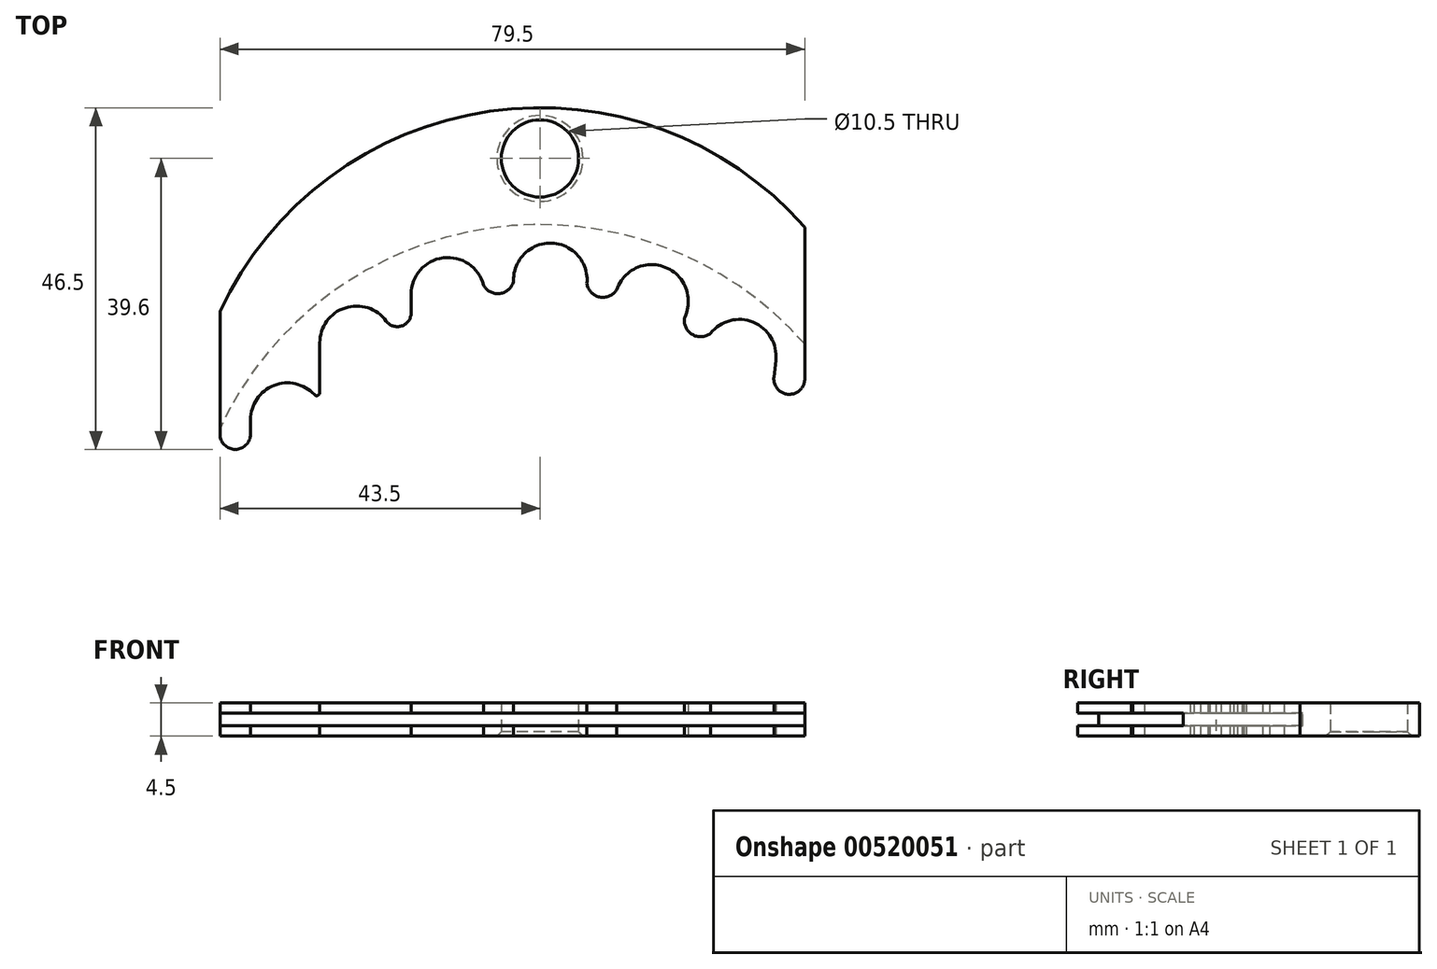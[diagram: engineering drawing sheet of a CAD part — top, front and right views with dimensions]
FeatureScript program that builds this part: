
annotation { "Feature Type Name" : "Feature", "Feature Type Description" : "" }
export const myFeature = defineFeature(function(context is Context, id is Id, definition is map)
    precondition{}
    {
        {
            var Q0;
            Q0=qCreatedBy(makeId("Top.planeOp"),FACE);
            var sketch = newSketch(context, id + "F0", { "sketchPlane" : qUnion([Q0])});
            skCircle(sketch, "E0", {"center": v(0, 0) * mm, "radius": 13 * mm, "construction": true});
            skCircle(sketch, "E1", {"center": v(0, 0) * mm, "radius": 13.5 * mm, "construction": true});
            skCircle(sketch, "E2", {"center": v(0, 0) * mm, "radius": 16 * mm, "construction": true});
            skLineSegment(sketch, "E3", {"start": v(0, 0) * mm, "end": v(0.47, 13.5) * mm, "construction": true});
            skLineSegment(sketch, "E4", {"start": v(0, 0) * mm, "end": v(5.06, 12.52) * mm, "construction": true});
            skLineSegment(sketch, "E5", {"start": v(0, 0) * mm, "end": v(9.03, 10.03) * mm, "construction": true});
            skLineSegment(sketch, "E6", {"start": v(0, 0) * mm, "end": v(-4.17, 12.84) * mm, "construction": true});
            skLineSegment(sketch, "E7", {"start": v(0, 0) * mm, "end": v(-8.31, 10.64) * mm, "construction": true});
            skLineSegment(sketch, "E8", {"start": v(0, 0) * mm, "end": v(-11.45, 7.15) * mm, "construction": true});
            skArc(sketch, "E9", {"start": v(2.13, 13.33) * mm, "mid": v(0.53, 15.16) * mm, "end": v(-1.2, 13.45) * mm});
            skArc(sketch, "E10", {"start": v(6.56, 11.8) * mm, "mid": v(5.68, 14.06) * mm, "end": v(3.48, 13.04) * mm});
            skArc(sketch, "E11", {"start": v(10.69, 9.85) * mm, "mid": v(9.67, 11.57) * mm, "end": v(7.73, 11.07) * mm});
            skArc(sketch, "E12", {"start": v(-2.56, 13.26) * mm, "mid": v(-4.38, 14.5) * mm, "end": v(-5.84, 12.84) * mm});
            skArc(sketch, "E13", {"start": v(-6.94, 11.58) * mm, "mid": v(-8.8, 12.23) * mm, "end": v(-9.98, 10.64) * mm});
            skArc(sketch, "E14", {"start": v(-10.23, 8.29) * mm, "mid": v(-12.06, 8.7) * mm, "end": v(-13.12, 7.15) * mm});
            skArc(sketch, "E15", {"start": v(-2.56, 13.26) * mm, "mid": v(-1.8, 12.87) * mm, "end": v(-1.2, 13.45) * mm});
            skArc(sketch, "E16", {"start": v(2.13, 13.33) * mm, "mid": v(2.7, 12.72) * mm, "end": v(3.48, 13.04) * mm});
            skArc(sketch, "E17", {"start": v(6.56, 11.8) * mm, "mid": v(6.89, 11.02) * mm, "end": v(7.73, 11.07) * mm});
            skLineSegment(sketch, "E18", {"start": v(-5.84, 12.84) * mm, "end": v(-5.84, 12) * mm});
            skLineSegment(sketch, "E19", {"start": v(-6.97, 11.62) * mm, "end": v(-6.97, 11.62) * mm});
            skArc(sketch, "E20", {"start": v(-6.97, 11.62) * mm, "mid": v(-6.27, 11.4) * mm, "end": v(-5.84, 12) * mm});
            skLineSegment(sketch, "E21", {"start": v(-9.98, 10.64) * mm, "end": v(-9.98, 8.38) * mm});
            skArc(sketch, "E22", {"start": v(-10.23, 8.29) * mm, "mid": v(-10.07, 8.25) * mm, "end": v(-9.98, 8.38) * mm});
            skArc(sketch, "E23", {"start": v(-14.5, 6.5) * mm, "mid": v(-13.8, 5.8) * mm, "end": v(-13.12, 6.5) * mm});
            skArc(sketch, "E24", {"start": v(10.6, 9.08) * mm, "mid": v(11.26, 8.3) * mm, "end": v(12, 9) * mm});
            skLineSegment(sketch, "E25", {"start": v(-14.5, 0) * mm, "end": v(-14.5, 12.06) * mm});
            skLineSegment(sketch, "E26", {"start": v(12, 0) * mm, "end": v(12, 15.88) * mm});
            skArc(sketch, "E27", {"start": v(12, 15.88) * mm, "mid": v(-2.28, 21.14) * mm, "end": v(-14.5, 12.06) * mm});
            skLineSegment(sketch, "E28", {"start": v(-13.12, 7.15) * mm, "end": v(-13.12, 6.5) * mm});
            skLineSegment(sketch, "E29", {"start": v(-14.5, 19) * mm, "end": v(12, 19) * mm, "construction": true});
            skLineSegment(sketch, "E30", {"start": v(10.69, 9.85) * mm, "end": v(10.6, 9.08) * mm});
            skCircle(sketch, "E31", {"center": v(0, 19) * mm, "radius": 1.75 * mm});
            skSolve(sketch);
        }
        {
            var Q0;
            Q0=makeQuery(id+"F0.imprint","IMPRINT",FACE,{"disambiguationData":[TD([[makeQuery(id+"F0.imprint","IMPRINT",EDGE,{"derivedFrom":sQuery(id+"F0.wireOp",EDGE,"E9")}),-1.0]])]});
            extrude(context, id + "F1", {"entities" : qUnion([Q0]), "endBound" : BoundingType.SYMMETRIC, "depth" : 1.5 * mm});
        }
        {
            var Q0;
            Q0=makeQuery(id+"F1.opExtrude","CAP_EDGE",EDGE,{"disambiguationData":[OSD([sQuery(id+"F0.wireOp",EDGE,"E31")])],"isStart":true});
            chamfer(context, id + "F2", {"entities" : qUnion([Q0]), "width" : 0.2 * mm, "tangentPropagation" : true});
        }
        {
            var Q0;
            Q0=qCreatedBy(makeId("Top.planeOp"),FACE);
            var sketch = newSketch(context, id + "F3", { "sketchPlane" : qUnion([Q0])});
            skCircle(sketch, "E32", {"center": v(0, 0) * mm, "radius": 16 * mm});
            skSolve(sketch);
        }
        {
            var Q0;
            Q0=makeQuery(id+"F3.imprint","IMPRINT",FACE,{"disambiguationData":[TD([[makeQuery(id+"F3.imprint","IMPRINT",EDGE,{"derivedFrom":sQuery(id+"F3.wireOp",EDGE,"E32")}),1.0]])]});
            extrude(context, id + "F4", {"entities" : qUnion([Q0]), "operationType" : NewBodyOperationType.REMOVE, "endBound" : BoundingType.SYMMETRIC, "oppositeDirection" : true, "depth" : (0.5 + (0.1 + 0.09) / 3) * mm});
        }
        {
            var Q0;
            Q0=makeQuery(id+"F1.opExtrude","SWEPT_BODY",BODY,{"disambiguationData":[OSD([sQuery(id+"F0.wireOp",EDGE,"E9"),sQuery(id+"F0.wireOp",EDGE,"E10"),sQuery(id+"F0.wireOp",EDGE,"E11"),sQuery(id+"F0.wireOp",EDGE,"E12"),sQuery(id+"F0.wireOp",EDGE,"E13"),sQuery(id+"F0.wireOp",EDGE,"E14"),sQuery(id+"F0.wireOp",EDGE,"E15"),sQuery(id+"F0.wireOp",EDGE,"E16"),sQuery(id+"F0.wireOp",EDGE,"E17"),sQuery(id+"F0.wireOp",EDGE,"E18"),sQuery(id+"F0.wireOp",EDGE,"E20"),sQuery(id+"F0.wireOp",EDGE,"E21"),sQuery(id+"F0.wireOp",EDGE,"E22"),sQuery(id+"F0.wireOp",EDGE,"E23"),sQuery(id+"F0.wireOp",EDGE,"E24"),sQuery(id+"F0.wireOp",EDGE,"E25"),sQuery(id+"F0.wireOp",EDGE,"E26"),sQuery(id+"F0.wireOp",EDGE,"E27"),sQuery(id+"F0.wireOp",EDGE,"E28"),sQuery(id+"F0.wireOp",EDGE,"E30"),sQuery(id+"F0.wireOp",EDGE,"E31")])]});
            var Q1;
            Q1=qCreatedBy(makeId("Origin.pointOp"),VERTEX);
            transform(context, id + "F5", {"entities" : qUnion([Q0]), "transformType" : TransformType.SCALE_UNIFORMLY, "scale" : 3, "makeCopy" : false, "scalePoint" : qUnion([Q1])});
        }
    });
